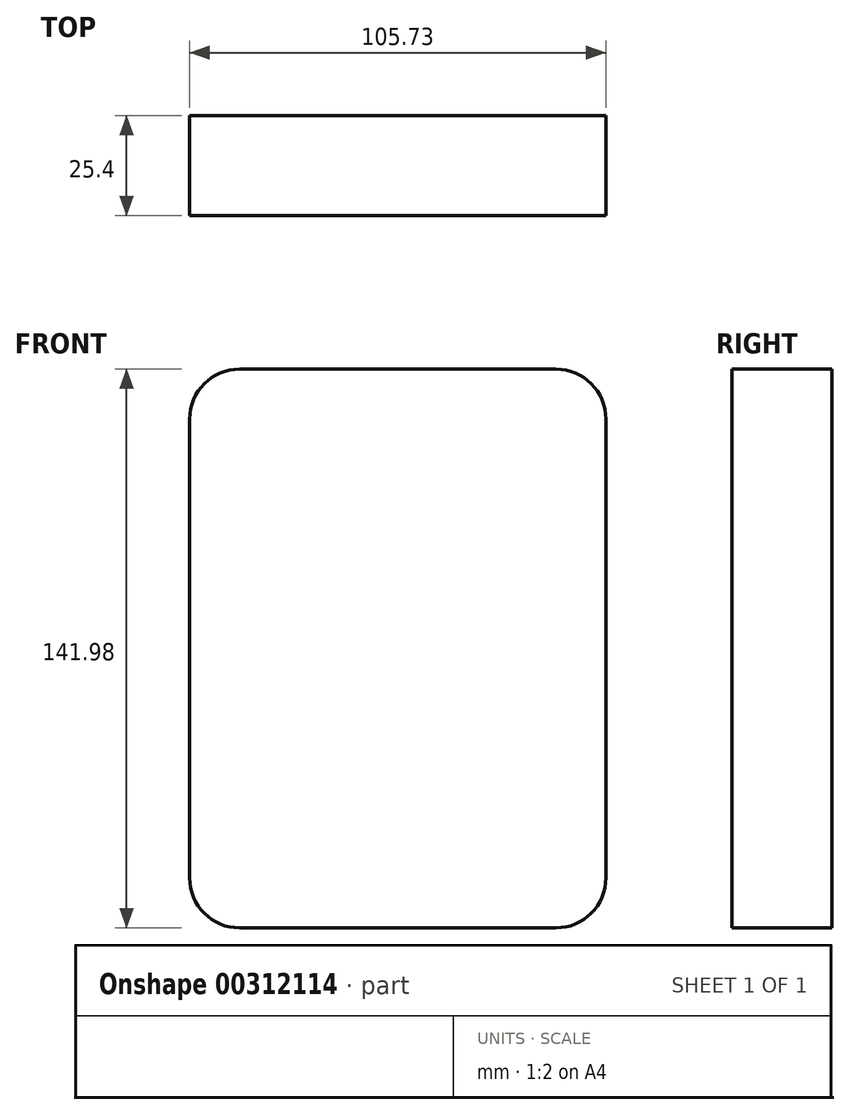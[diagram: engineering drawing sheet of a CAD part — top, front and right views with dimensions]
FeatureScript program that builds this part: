
annotation { "Feature Type Name" : "Feature", "Feature Type Description" : "" }
export const myFeature = defineFeature(function(context is Context, id is Id, definition is map)
    precondition{}
    {
        {
            var Q0;
            Q0=qCreatedBy(makeId("Front.planeOp"),FACE);
            var sketch = newSketch(context, id + "F0", { "sketchPlane" : qUnion([Q0])});
            skLineSegment(sketch, "E0.bottom", {"start": v(-37.87, 61.79) * mm, "end": v(42.46, 61.79) * mm});
            skLineSegment(sketch, "E0.top", {"start": v(-37.87, -80.19) * mm, "end": v(42.46, -80.19) * mm});
            skLineSegment(sketch, "E0.left", {"start": v(-50.57, 49.09) * mm, "end": v(-50.57, -67.49) * mm});
            skLineSegment(sketch, "E0.right", {"start": v(55.16, 49.09) * mm, "end": v(55.16, -67.49) * mm});
            skPoint(sketch, "E1.visualSharp", {"position": v(-50.57, 61.79) * mm});
            skArc(sketch, "E1.filletArc", {"start": v(-37.87, 61.79) * mm, "mid": v(-46.85, 58.07) * mm, "end": v(-50.57, 49.09) * mm});
            skPoint(sketch, "E2.visualSharp", {"position": v(55.16, 61.79) * mm});
            skArc(sketch, "E2.filletArc", {"start": v(55.16, 49.09) * mm, "mid": v(51.44, 58.07) * mm, "end": v(42.46, 61.79) * mm});
            skPoint(sketch, "E3.visualSharp", {"position": v(55.16, -80.19) * mm});
            skArc(sketch, "E3.filletArc", {"start": v(42.46, -80.19) * mm, "mid": v(51.44, -76.47) * mm, "end": v(55.16, -67.49) * mm});
            skPoint(sketch, "E4.visualSharp", {"position": v(-50.57, -80.19) * mm});
            skArc(sketch, "E4.filletArc", {"start": v(-50.57, -67.49) * mm, "mid": v(-46.85, -76.47) * mm, "end": v(-37.87, -80.19) * mm});
            skSolve(sketch);
        }
        {
            var Q0;
            Q0 = qSketchRegion(id + "F0", true);
            extrude(context, id + "F1", {"entities" : qUnion([Q0]), "depth" : 25.4 * mm});
        }
    });
